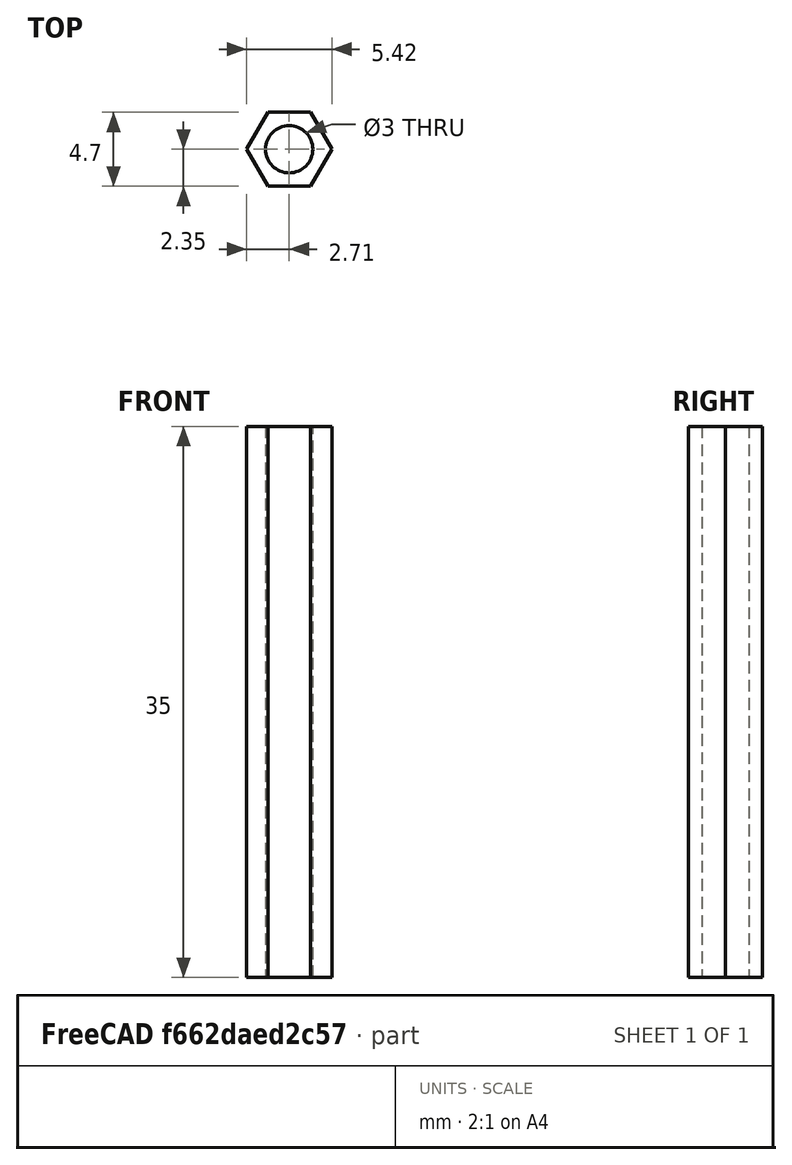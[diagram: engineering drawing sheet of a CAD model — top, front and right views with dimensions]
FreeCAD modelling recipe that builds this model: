
FCSTD DOCUMENT  (FreeCAD 0.18.4R)
Label: coxial_M3_35mm
License: All rights reserved
LicenseURL: http://en.wikipedia.org/wiki/All_rights_reserved
objects: Sketcher::SketchObject×1, PartDesign::Pad×1, PartDesign::Body×1
note: 4 computed .brp shape members not serialized (recipe doc carries the construction recipe); baked Part::Feature solids carry a one-line shape summary decoded from their .brp

FEATURE [Sketcher::SketchObject] Sketch
  MapMode = 5
  Support = -> [XY_Plane]
  sketch-geometry (8):
    g0: Circle CenterX=0 CenterY=0 CenterZ=0 NormalX=0 NormalY=0 NormalZ=1 AngleXU=0 Radius=1.5
    g1: LineSegment StartX=1.35677 StartY=-2.35 StartZ=0 EndX=2.71355 EndY=0 EndZ=0
    g2: LineSegment StartX=2.71355 StartY=0 StartZ=0 EndX=1.35677 EndY=2.35 EndZ=0
    g3: LineSegment StartX=1.35677 StartY=2.35 StartZ=0 EndX=-1.35677 EndY=2.35 EndZ=0
    g4: LineSegment StartX=-1.35677 StartY=2.35 StartZ=0 EndX=-2.71355 EndY=-4e-16 EndZ=0
    g5: LineSegment StartX=-2.71355 StartY=-5e-16 StartZ=0 EndX=-1.35677 EndY=-2.35 EndZ=0
    g6: LineSegment StartX=-1.35677 StartY=-2.35 StartZ=0 EndX=1.35677 EndY=-2.35 EndZ=0
    g7: Circle [constr] CenterX=0 CenterY=0 CenterZ=0 NormalX=0 NormalY=0 NormalZ=1 AngleXU=0 Radius=2.71355
  constraints (18):
    c: Coincident(g0,g-1)
    c: Radius(g0) = 1.5
    c: Coincident(g1,g2)
    c: Coincident(g2,g3)
    c: Coincident(g3,g4)
    c: Coincident(g4,g5)
    c: Coincident(g5,g6)
    c: Coincident(g6,g1)
    c: Equal(g1, g2-g6) x5
    c: PointOnObject(g1,g7)
    c: PointOnObject(g2,g7)
    c: PointOnObject(g3,g7)
    c: PointOnObject(g4,g7)
    c: PointOnObject(g5,g7)
    c: PointOnObject(g6,g7)
    c: Distance(g2,g4) = 4.7
    c: Coincident(g7,g0)
    c: Horizontal(g3)
FEATURE [PartDesign::Pad] Pad
  Length = 35
  Length2 = 100
  Profile = -> Sketch
  Type = 0
FEATURE [PartDesign::Body] Body
  Group = -> [Sketch,Pad]
  Origin = -> Origin
  Tip = -> Pad
